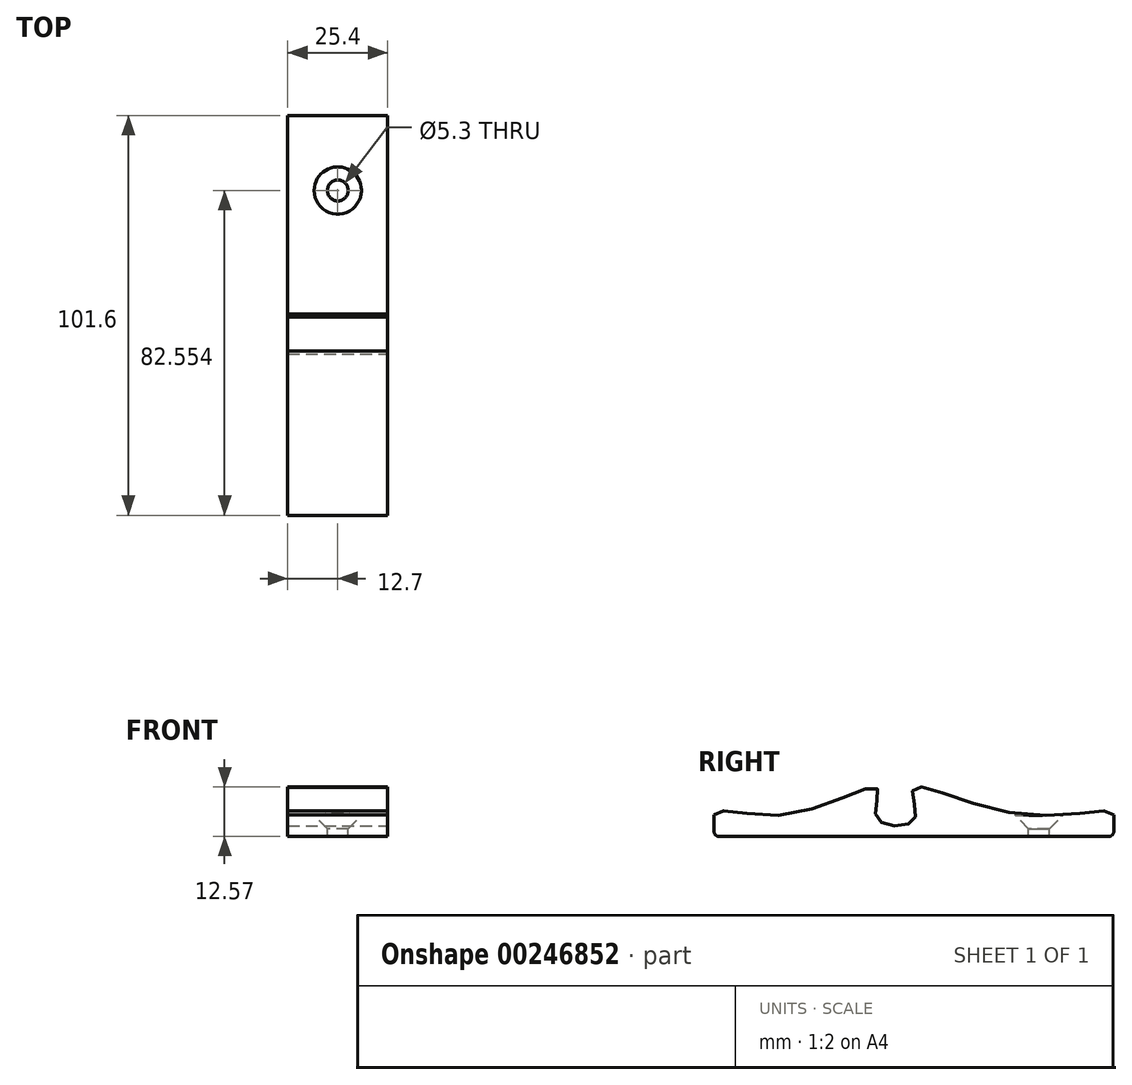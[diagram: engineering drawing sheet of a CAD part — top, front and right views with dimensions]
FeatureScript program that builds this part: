
annotation { "Feature Type Name" : "Feature", "Feature Type Description" : "" }
export const myFeature = defineFeature(function(context is Context, id is Id, definition is map)
    precondition{}
    {
        {
            var Q0;
            Q0=qCreatedBy(makeId("Right.planeOp"),FACE);
            var sketch = newSketch(context, id + "F0", { "sketchPlane" : qUnion([Q0])});
            skLineSegment(sketch, "E0.top", {"start": v(-29.52, -6.68) * mm, "end": v(69.46, -6.68) * mm});
            skLineSegment(sketch, "E0.left", {"start": v(-30.76, -1.15) * mm, "end": v(-30.76, -5.44) * mm});
            skLineSegment(sketch, "E0.right", {"start": v(70.84, -1.15) * mm, "end": v(70.84, -5.3) * mm});
            skPoint(sketch, "E1.visualSharp", {"position": v(-30.76, 5.04) * mm});
            skPoint(sketch, "E2.visualSharp", {"position": v(-30.76, -6.68) * mm});
            skArc(sketch, "E2.filletArc", {"start": v(-30.76, -5.44) * mm, "mid": v(-30.4, -6.31) * mm, "end": v(-29.52, -6.68) * mm});
            skPoint(sketch, "E3.visualSharp", {"position": v(70.84, 5.04) * mm});
            skPoint(sketch, "E4.visualSharp", {"position": v(70.84, -6.68) * mm});
            skArc(sketch, "E4.filletArc", {"start": v(69.46, -6.68) * mm, "mid": v(70.44, -6.27) * mm, "end": v(70.84, -5.3) * mm});
            skFitSpline(sketch, "E5", {"points": [v(-30.76, -1.15) * mm, v(-12.67, -1.15) * mm, v(10.63, 5.55) * mm, v(10.24, 0) * mm, v(12.2, -3.33) * mm, v(19.07, -3.33) * mm, v(20.4, 0) * mm, v(20.03, 5.55) * mm, v(47.8, -1.15) * mm, v(70.84, -1.15) * mm], "startDerivative": vector(1.82, 57.2) * mm, "endDerivative": vector(4.24, -48.75) * mm});
            skPoint(sketch, "E3.filletArc.center.orphan", {"position": v(64.6, -1.15) * mm});
            skLineSegment(sketch, "E6", {"start": v(6.17, -3.33) * mm, "end": v(27.32, -3.33) * mm, "construction": true});
            skLineSegment(sketch, "E7", {"start": v(4.74, 5.55) * mm, "end": v(29.36, 5.55) * mm, "construction": true});
            skSolve(sketch);
        }
        {
            var Q0;
            Q0 = qSketchRegion(id + "F0", true);
            extrude(context, id + "F1", {"entities" : qUnion([Q0]), "depth" : 25.4 * mm});
        }
        {
            var Q0;
            Q0=qCreatedBy(makeId("Top.planeOp"),FACE);
            var sketch = newSketch(context, id + "F2", { "sketchPlane" : qUnion([Q0])});
            skPoint(sketch, "E8", {"position": v(12.7, 51.8) * mm});
            skSolve(sketch);
        }
        {
            var Q0;
            Q0=sQuery(id+"F2.wireOp",VERTEX,"E8");
            var Q1;
            Q1=makeQuery(id+"F1.opExtrude","SWEPT_BODY",BODY,{"disambiguationData":[OSD([sQuery(id+"F0.wireOp",EDGE,"E0.top"),sQuery(id+"F0.wireOp",EDGE,"E0.left"),sQuery(id+"F0.wireOp",EDGE,"E0.right"),sQuery(id+"F0.wireOp",EDGE,"E2.filletArc"),sQuery(id+"F0.wireOp",EDGE,"E4.filletArc"),sQuery(id+"F0.wireOp",EDGE,"E5")])]});
            hole(context, id + "F3", {"style" : HoleStyle.C_SINK, "endStyle" : HoleEndStyle.BLIND, "holeDiameter" : 5.3 * mm, "cSinkDiameter" : 12 * mm, "cSinkAngle" : 90 * degree, "holeDepth" : 50.8 * mm, "tappedDepth" : 12.7 * mm, "tapClearance" : 3, "locations" : qUnion([Q0]), "scope" : qUnion([Q1])});
        }
    });
